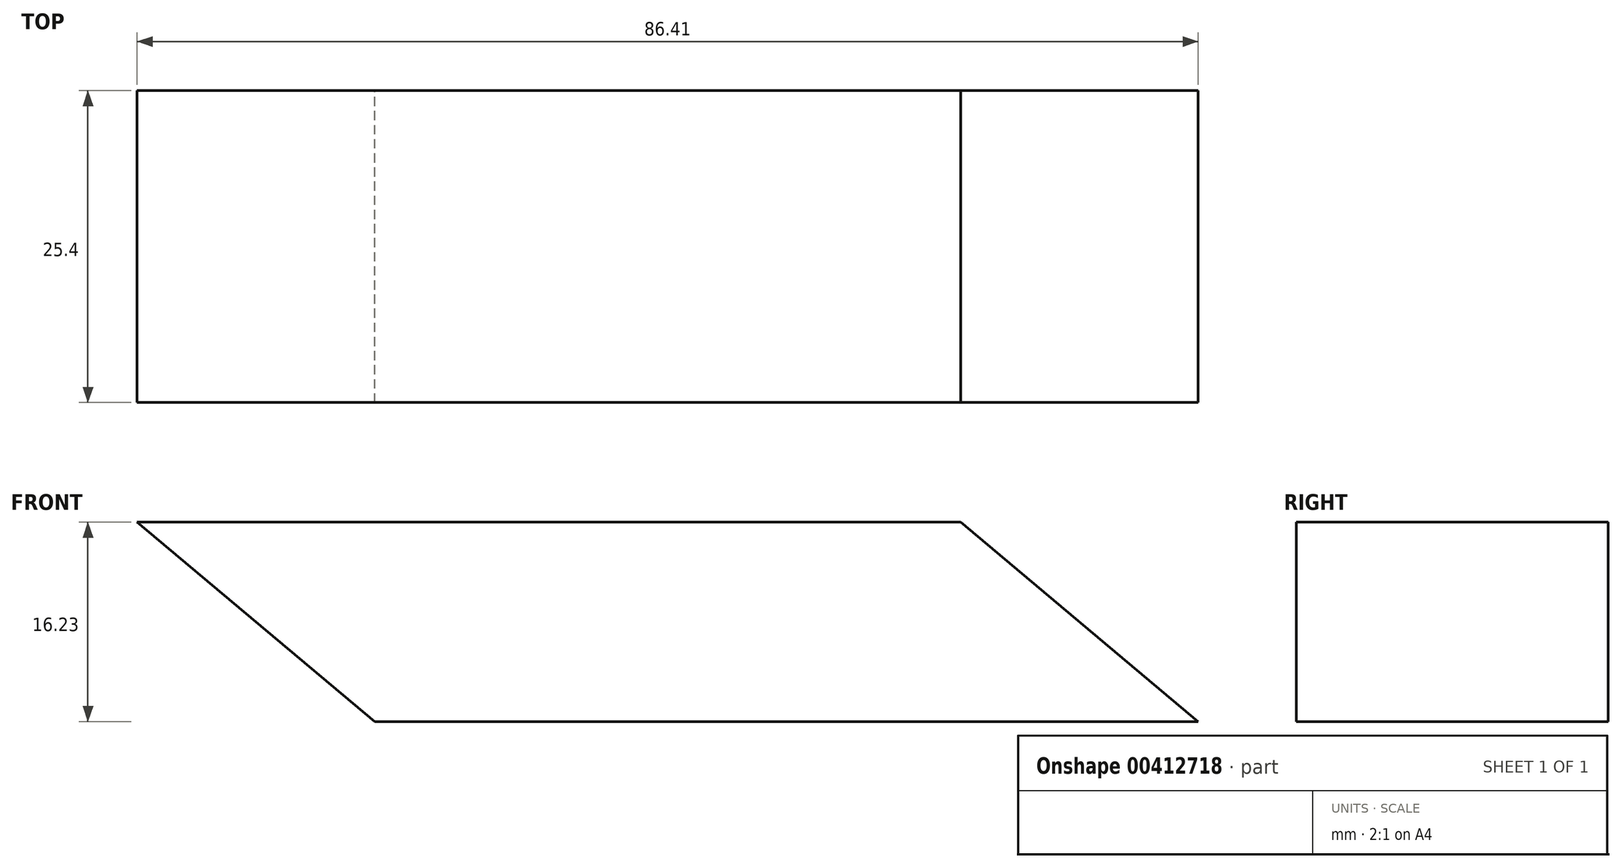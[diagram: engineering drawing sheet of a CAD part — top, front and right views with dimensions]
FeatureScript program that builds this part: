
annotation { "Feature Type Name" : "Feature", "Feature Type Description" : "" }
export const myFeature = defineFeature(function(context is Context, id is Id, definition is map)
    precondition{}
    {
        {
            var Q0;
            Q0=qCreatedBy(makeId("Front.planeOp"),FACE);
            var sketch = newSketch(context, id + "F0", { "sketchPlane" : qUnion([Q0])});
            skLineSegment(sketch, "E0.bottom", {"start": v(-48.8, 16.23) * mm, "end": v(18.28, 16.23) * mm});
            skLineSegment(sketch, "E0.top", {"start": v(-29.45, 0) * mm, "end": v(37.62, 0) * mm});
            skLineSegment(sketch, "E0.left", {"start": v(-48.8, 16.23) * mm, "end": v(-29.45, 0) * mm});
            skLineSegment(sketch, "E0.right", {"start": v(18.28, 16.23) * mm, "end": v(37.62, 0) * mm});
            skSolve(sketch);
        }
        {
            var Q0;
            Q0 = qSketchRegion(id + "F0", true);
            extrude(context, id + "F1", {"entities" : qUnion([Q0]), "depth" : 25.4 * mm});
        }
    });
